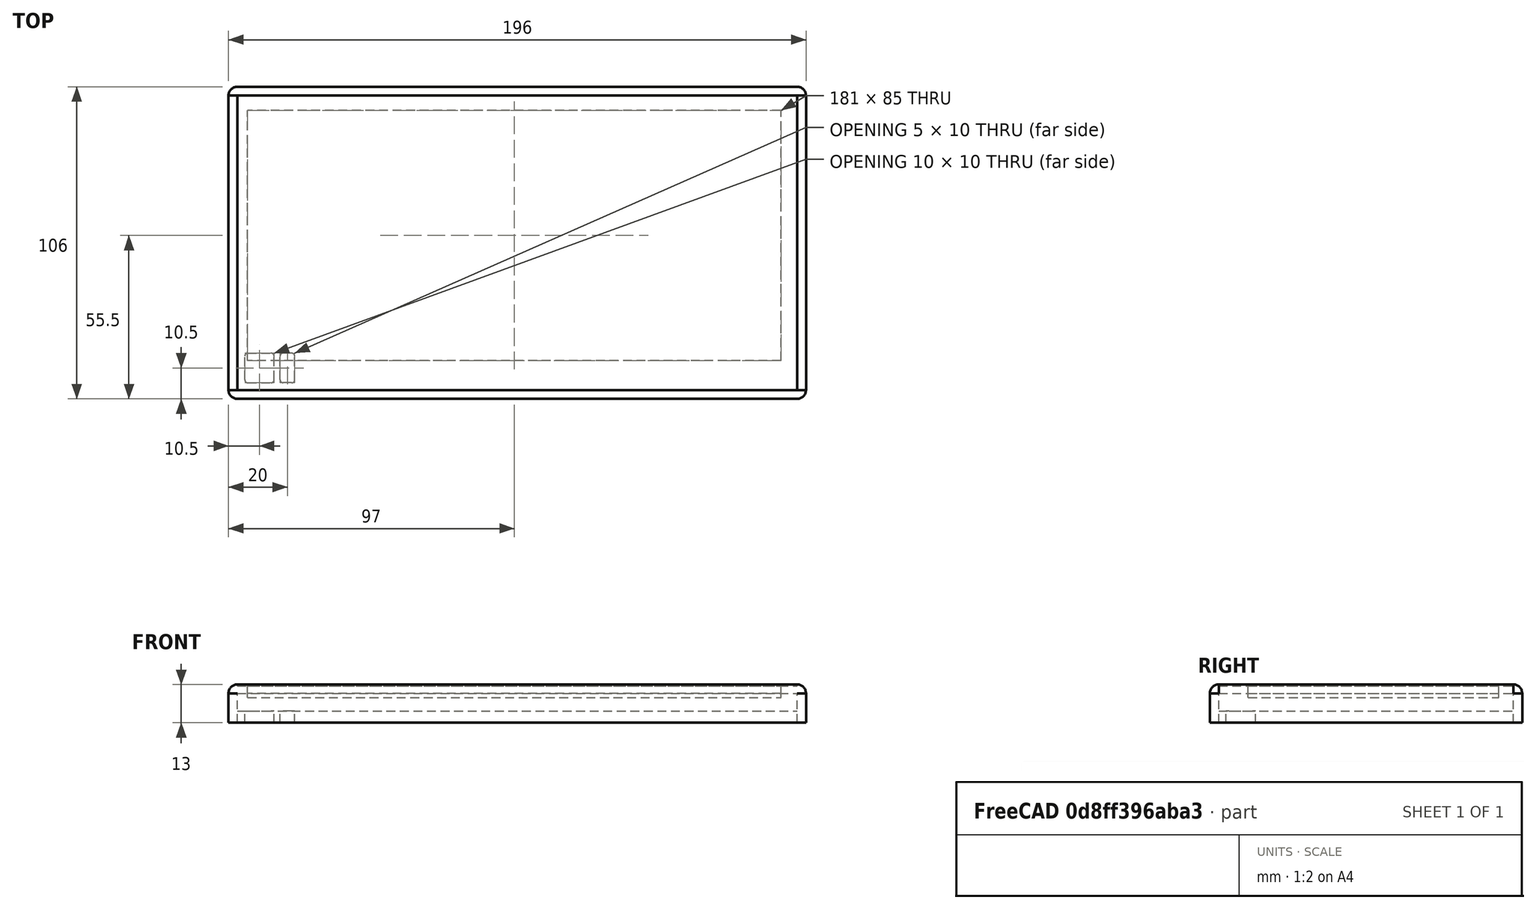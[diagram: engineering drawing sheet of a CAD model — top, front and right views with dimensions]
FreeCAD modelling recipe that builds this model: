
FCSTD DOCUMENT  (FreeCAD 0.15R4671 (Git))
Label: Tablet-will-renamed-2015-with-ubuntu
License: All rights reserved
LicenseURL: http://es.wikipedia.org/wiki/Todos_los_derechos_reservados
objects: Part::Box×10, Part::Fillet×4, Part::Cut×4, Part::Thickness×1
note: 19 computed .brp shape members not serialized (recipe doc carries the construction recipe); baked Part::Feature solids carry a one-line shape summary decoded from their .brp

FEATURE [Part::Box] Box  label="Cubo"
  Height = 10
  Length = 190
  Width = 100
FEATURE [Part::Thickness] Thickness
  Faces = -> Box [Face5]
  Intersection = false
  Join = 0
  Mode = 0
  SelfIntersection = false
  Value = 3
FEATURE [Part::Box] Box001  label="Cubo001"
  Height = 4
  Length = 190
  Width = 100
FEATURE [Part::Box] Box003  label="Cubo003"
  Height = 10
  Length = 10
  Placement = pos=(2.5,2.5,-4) rot=(0,0,1;0rad)
  Width = 10
FEATURE [Part::Fillet] Fillet001
  Base = -> Box003
  Edges = 4 edges r=1: [Edge1,Edge3,Edge5,Edge7]
  Placement = pos=(0,0,-2) rot=(0,0,1;0rad)
FEATURE [Part::Cut] Cut
  Base = -> Box001
  Tool = -> Fillet001
FEATURE [Part::Box] Box004  label="Cubo004"
  Height = 4
  Length = 10
  Placement = pos=(2.5,2.5,1) rot=(0,0,1;0rad)
  Width = 10
FEATURE [Part::Fillet] Fillet
  Base = -> Box004
  Edges = 4 edges r=1: [Edge1,Edge3,Edge5,Edge7]
  Placement = pos=(0,0,-1) rot=(0,0,1;0rad)
FEATURE [Part::Box] Box005  label="Cubo005"
  Height = 9
  Length = 5
  Placement = pos=(14.5,2.5,-2) rot=(0,0,1;0rad)
  Width = 10
FEATURE [Part::Fillet] Fillet002
  Base = -> Box005
  Edges = 4 edges r=1: [Edge1,Edge3,Edge5,Edge7]
FEATURE [Part::Cut] Cut001
  Base = -> Cut
  Tool = -> Fillet002
FEATURE [Part::Box] Box006  label="Cubo006"
  Height = 4
  Length = 5
  Placement = pos=(14.5,2.5,-2) rot=(0,0,1;0rad)
  Width = 10
FEATURE [Part::Fillet] Fillet003
  Base = -> Box006
  Edges = 4 edges r=1: [Edge1,Edge3,Edge5,Edge7]
  Placement = pos=(0,0,2) rot=(0,0,1;0rad)
FEATURE [Part::Box] Box007  label="Cubo007"
  Height = 1
  Length = 190
  Placement = pos=(0,0,12.5) rot=(0,0,1;0rad)
  Width = 100
FEATURE [Part::Cut] Cut002
  Base = -> Thickness
  Tool = -> Box007
FEATURE [Part::Box] Box008  label="Cubo008"
  Height = 0.5
  Length = 190
  Placement = pos=(0,0,12.5) rot=(0,0,1;0rad)
  Width = 100
FEATURE [Part::Box] Box009  label="Cubo009"
  Height = 4
  Length = 181
  Placement = pos=(3.5,10,8.5) rot=(0,0,1;0rad)
  Width = 85
FEATURE [Part::Box] Box010  label="Cubo010"
  Height = 4
  Length = 181
  Placement = pos=(3.5,10,8.5) rot=(0,0,1;0rad)
  Width = 85
FEATURE [Part::Cut] Cut003
  Base = -> Cut002
  Tool = -> Box009
